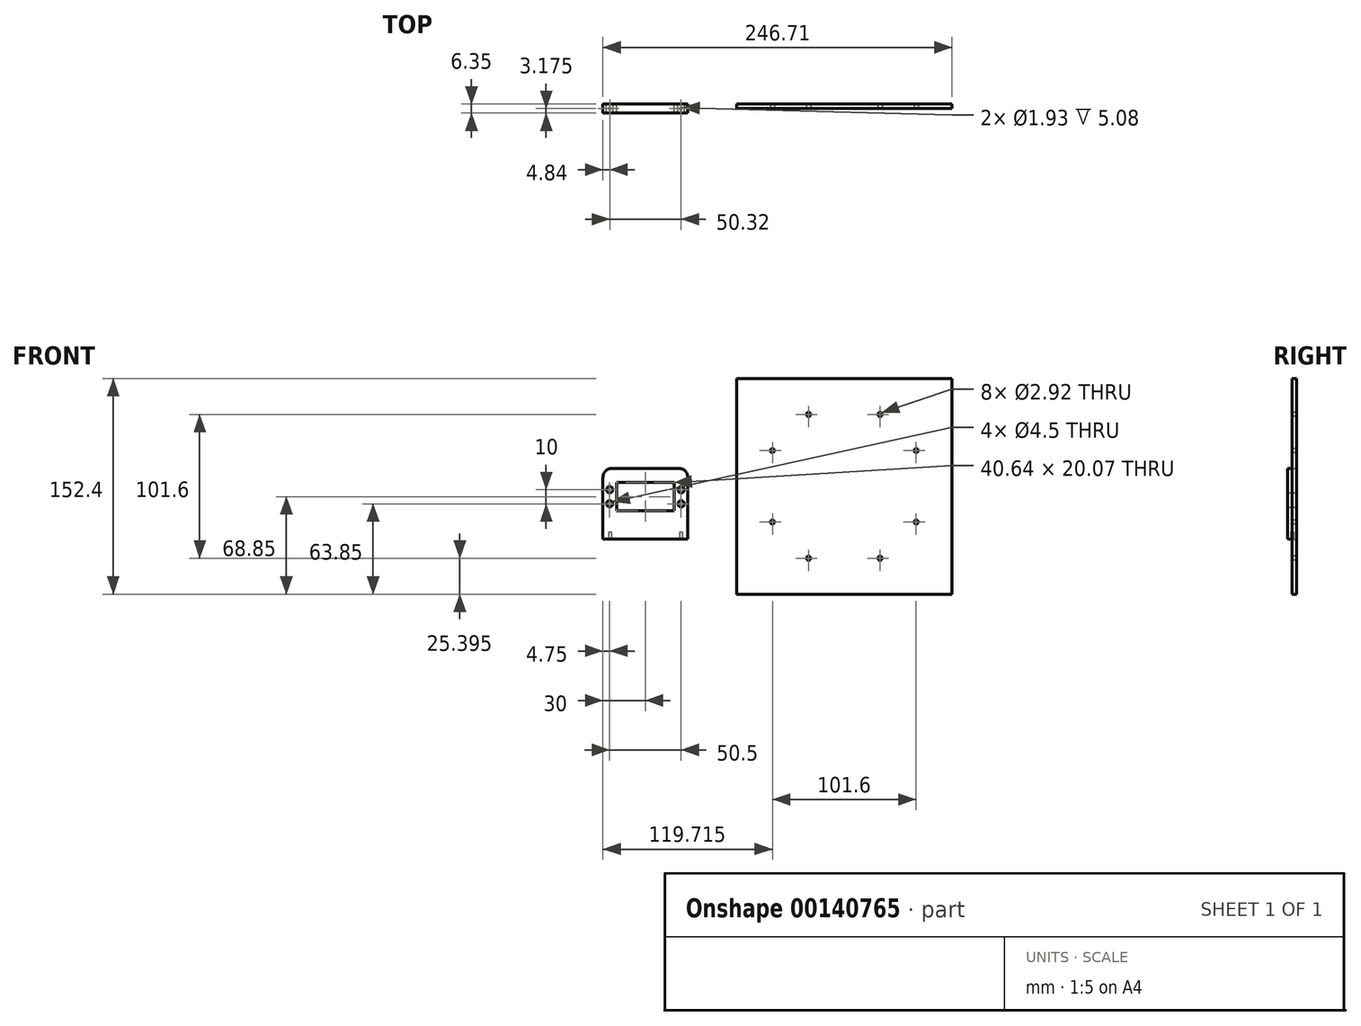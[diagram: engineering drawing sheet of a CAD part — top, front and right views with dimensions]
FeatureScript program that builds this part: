
annotation { "Feature Type Name" : "Feature", "Feature Type Description" : "" }
export const myFeature = defineFeature(function(context is Context, id is Id, definition is map)
    precondition{}
    {
        {
            var Q0;
            Q0=qCreatedBy(makeId("Front.planeOp"),FACE);
            var sketch = newSketch(context, id + "F0", { "sketchPlane" : qUnion([Q0])});
            skPoint(sketch, "E0.middle", {"position": v(0, 0) * mm});
            skCircle(sketch, "E1", {"center": v(-25.25, 5) * mm, "radius": 2.25 * mm});
            skCircle(sketch, "E2", {"center": v(-25.25, -4.97) * mm, "radius": 2.25 * mm});
            skPoint(sketch, "E3.endSnap0", {"position": v(0, 5) * mm});
            skCircle(sketch, "E4.MirrorC", {"center": v(25.25, 5) * mm, "radius": 2.25 * mm});
            skCircle(sketch, "E5.MirrorC", {"center": v(25.25, -5) * mm, "radius": 2.25 * mm});
            skLineSegment(sketch, "E6.bottom", {"start": v(20.32, 10.03) * mm, "end": v(-20.32, 10.03) * mm});
            skLineSegment(sketch, "E6.top", {"start": v(20.32, -10.03) * mm, "end": v(-20.32, -10.03) * mm});
            skLineSegment(sketch, "E6.left", {"start": v(20.32, 10.03) * mm, "end": v(20.32, -10.03) * mm});
            skLineSegment(sketch, "E6.right", {"start": v(-20.32, 10.03) * mm, "end": v(-20.32, -10.03) * mm});
            skLineSegment(sketch, "E7.top", {"start": v(23.65, 20.03) * mm, "end": v(-23.65, 20.03) * mm});
            skLineSegment(sketch, "E8", {"start": v(30, 13.68) * mm, "end": v(30, -29.97) * mm});
            skLineSegment(sketch, "E9", {"start": v(30, -29.97) * mm, "end": v(-30, -29.97) * mm});
            skLineSegment(sketch, "E10", {"start": v(-30, -29.97) * mm, "end": v(-30, 13.68) * mm});
            skLineSegment(sketch, "E11", {"start": v(25.25, -29.97) * mm, "end": v(25.25, -24.89) * mm});
            skLineSegment(sketch, "E12", {"start": v(-25.25, -29.97) * mm, "end": v(-25.25, -24.89) * mm});
            skPoint(sketch, "E13.visualSharp", {"position": v(-30, 20.03) * mm});
            skArc(sketch, "E13.filletArc", {"start": v(-23.65, 20.03) * mm, "mid": v(-28.14, 18.17) * mm, "end": v(-30, 13.68) * mm});
            skPoint(sketch, "E14.visualSharp", {"position": v(30, 20.03) * mm});
            skArc(sketch, "E14.filletArc", {"start": v(30, 13.68) * mm, "mid": v(28.14, 18.17) * mm, "end": v(23.65, 20.03) * mm});
            skSolve(sketch);
        }
        {
            var Q0;
            Q0=makeQuery(id+"F0.imprint","IMPRINT",FACE,{"disambiguationData":[TD([[makeQuery(id+"F0.imprint","IMPRINT",EDGE,{"derivedFrom":sQuery(id+"F0.wireOp",EDGE,"E1")}),-1.0]])]});
            extrude(context, id + "F1", {"entities" : qUnion([Q0]), "depth" : 6.35 * mm});
        }
        {
            var Q0;
            Q0=qCreatedBy(makeId("Front.planeOp"),FACE);
            var sketch = newSketch(context, id + "F2", { "sketchPlane" : qUnion([Q0])});
            skLineSegment(sketch, "E15.bottom", {"start": v(216.71, 83.55) * mm, "end": v(64.31, 83.55) * mm});
            skLineSegment(sketch, "E15.top", {"start": v(216.71, -68.85) * mm, "end": v(64.31, -68.85) * mm});
            skLineSegment(sketch, "E15.left", {"start": v(216.71, 83.55) * mm, "end": v(216.71, -68.85) * mm});
            skLineSegment(sketch, "E15.right", {"start": v(64.31, 83.55) * mm, "end": v(64.31, -68.85) * mm});
            skPoint(sketch, "E15.middle", {"position": v(140.51, 7.35) * mm});
            skSolve(sketch);
        }
        {
            var Q0;
            Q0 = qSketchRegion(id + "F2", true);
            extrude(context, id + "F3", {"entities" : qUnion([Q0]), "depth" : 3.17 * mm});
        }
        {
            var Q0;
            Q0=makeQuery(id+"F3.opExtrude","CAP_FACE",FACE,{"disambiguationData":[OSD([sQuery(id+"F2.wireOp",EDGE,"E15.bottom"),sQuery(id+"F2.wireOp",EDGE,"E15.top"),sQuery(id+"F2.wireOp",EDGE,"E15.left"),sQuery(id+"F2.wireOp",EDGE,"E15.right")])],"isStart":false});
            var sketch = newSketch(context, id + "F4", { "sketchPlane" : qUnion([Q0])});
            skLineSegment(sketch, "E16.0.0", {"start": v(216.71, -68.85) * mm, "end": v(216.71, 83.55) * mm});
            skLineSegment(sketch, "E16.0.1", {"start": v(216.71, 83.55) * mm, "end": v(64.31, 83.55) * mm});
            skLineSegment(sketch, "E16.0.2", {"start": v(64.31, 83.55) * mm, "end": v(64.31, -68.85) * mm});
            skLineSegment(sketch, "E16.0.3", {"start": v(64.31, -68.85) * mm, "end": v(216.71, -68.85) * mm});
            skCircle(sketch, "E17", {"center": v(89.71, 32.6) * mm, "radius": 1.46 * mm});
            skCircle(sketch, "E18", {"center": v(89.71, -17.9) * mm, "radius": 1.46 * mm});
            skCircle(sketch, "E19", {"center": v(191.31, -17.9) * mm, "radius": 1.46 * mm});
            skCircle(sketch, "E20", {"center": v(191.31, 32.6) * mm, "radius": 1.46 * mm});
            skCircle(sketch, "E21", {"center": v(165.76, 58.15) * mm, "radius": 1.46 * mm});
            skCircle(sketch, "E22", {"center": v(165.76, -43.45) * mm, "radius": 1.46 * mm});
            skCircle(sketch, "E23", {"center": v(115.26, -43.45) * mm, "radius": 1.46 * mm});
            skCircle(sketch, "E24", {"center": v(115.26, 58.15) * mm, "radius": 1.46 * mm});
            skSolve(sketch);
        }
        {
            var Q0;
            Q0=makeQuery(id+"F4.imprint","IMPRINT",FACE,{"disambiguationData":[TD([[makeQuery(id+"F4.imprint","IMPRINT",EDGE,{"derivedFrom":sQuery(id+"F4.wireOp",EDGE,"E20")}),1.0]])]});
            var Q1;
            Q1=makeQuery(id+"F4.imprint","IMPRINT",FACE,{"disambiguationData":[TD([[makeQuery(id+"F4.imprint","IMPRINT",EDGE,{"derivedFrom":sQuery(id+"F4.wireOp",EDGE,"E21")}),1.0]])]});
            var Q2;
            Q2=makeQuery(id+"F4.imprint","IMPRINT",FACE,{"disambiguationData":[TD([[makeQuery(id+"F4.imprint","IMPRINT",EDGE,{"derivedFrom":sQuery(id+"F4.wireOp",EDGE,"E24")}),1.0]])]});
            var Q3;
            Q3=makeQuery(id+"F4.imprint","IMPRINT",FACE,{"disambiguationData":[TD([[makeQuery(id+"F4.imprint","IMPRINT",EDGE,{"derivedFrom":sQuery(id+"F4.wireOp",EDGE,"E17")}),1.0]])]});
            var Q4;
            Q4=makeQuery(id+"F4.imprint","IMPRINT",FACE,{"disambiguationData":[TD([[makeQuery(id+"F4.imprint","IMPRINT",EDGE,{"derivedFrom":sQuery(id+"F4.wireOp",EDGE,"E18")}),1.0]])]});
            var Q5;
            Q5=makeQuery(id+"F4.imprint","IMPRINT",FACE,{"disambiguationData":[TD([[makeQuery(id+"F4.imprint","IMPRINT",EDGE,{"derivedFrom":sQuery(id+"F4.wireOp",EDGE,"E23")}),1.0]])]});
            var Q6;
            Q6=makeQuery(id+"F4.imprint","IMPRINT",FACE,{"disambiguationData":[TD([[makeQuery(id+"F4.imprint","IMPRINT",EDGE,{"derivedFrom":sQuery(id+"F4.wireOp",EDGE,"E22")}),1.0]])]});
            var Q7;
            Q7=makeQuery(id+"F4.imprint","IMPRINT",FACE,{"disambiguationData":[TD([[makeQuery(id+"F4.imprint","IMPRINT",EDGE,{"derivedFrom":sQuery(id+"F4.wireOp",EDGE,"E19")}),1.0]])]});
            extrude(context, id + "F5", {"entities" : qUnion([Q0, Q1, Q2, Q3, Q4, Q5, Q6, Q7]), "operationType" : NewBodyOperationType.REMOVE, "oppositeDirection" : true, "depth" : 25.4 * mm});
        }
        {
            var Q0;
            Q0=makeQuery(id+"F1.opExtrude","SWEPT_FACE",FACE,{"disambiguationData":[OSD([sQuery(id+"F0.wireOp",EDGE,"E9")])]});
            var sketch = newSketch(context, id + "F6", { "sketchPlane" : qUnion([Q0])});
            skCircle(sketch, "E25", {"center": v(-25.16, 3.17) * mm, "radius": 0.97 * mm});
            skCircle(sketch, "E26.MirrorC", {"center": v(25.16, 3.18) * mm, "radius": 0.97 * mm});
            skLineSegment(sketch, "E27.0", {"start": v(-30, 6.35) * mm, "end": v(-30, 0) * mm});
            skSolve(sketch);
        }
        {
            var Q0;
            Q0 = qSketchRegion(id + "F6", true);
            extrude(context, id + "F7", {"entities" : qUnion([Q0]), "operationType" : NewBodyOperationType.REMOVE, "oppositeDirection" : true, "depth" : 5.08 * mm});
        }
    });
